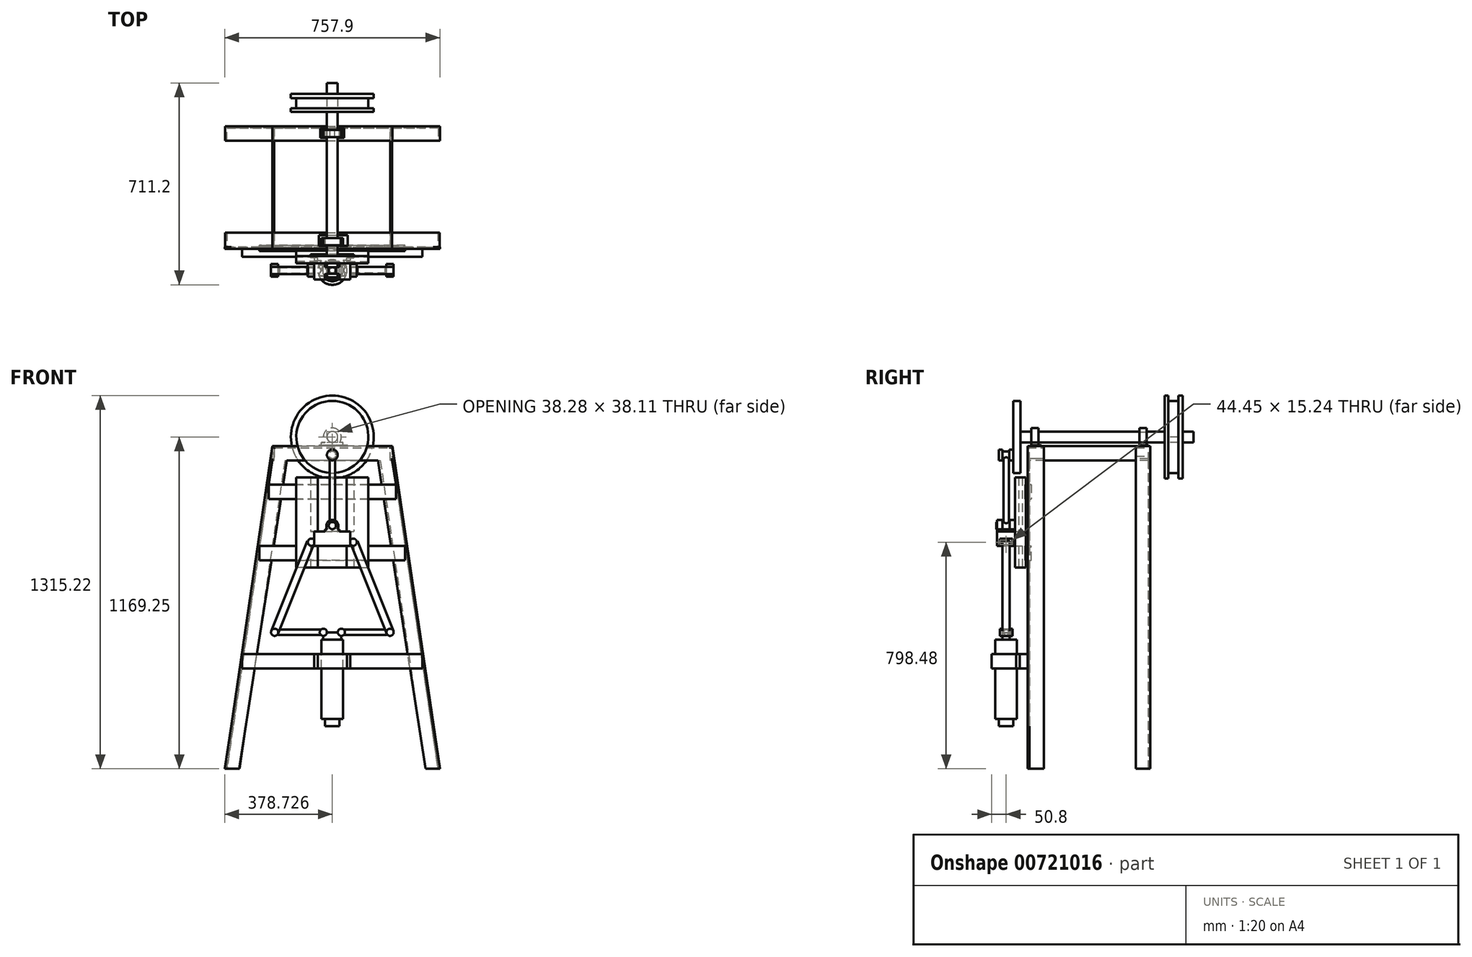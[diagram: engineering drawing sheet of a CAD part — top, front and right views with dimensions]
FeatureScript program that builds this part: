
annotation { "Feature Type Name" : "Feature", "Feature Type Description" : "" }
export const myFeature = defineFeature(function(context is Context, id is Id, definition is map)
    precondition{}
    {
        {
            var Q0;
            Q0=qCreatedBy(makeId("Top.planeOp"),FACE);
            cPlane(context, id + "F0", {"entities" : qUnion([Q0]), "cplaneType" : CPlaneType.OFFSET, "offset" : 127 * mm, "width" : 152.4 * mm, "height" : 152.4 * mm});
        }
        {
            var Q0;
            Q0=qCreatedBy(id+"F0.planeOp",FACE);
            var sketch = newSketch(context, id + "F1", { "sketchPlane" : qUnion([Q0])});
            skLineSegment(sketch, "E0", {"start": v(-31.75, 0) * mm, "end": v(-31.75, 12.7) * mm});
            skLineSegment(sketch, "E1", {"start": v(-31.75, 12.7) * mm, "end": v(-31.75, -12.7) * mm});
            skLineSegment(sketch, "E2", {"start": v(31.75, 0) * mm, "end": v(31.75, 12.7) * mm});
            skLineSegment(sketch, "E3", {"start": v(31.75, 12.7) * mm, "end": v(31.75, -12.7) * mm});
            skLineSegment(sketch, "E4", {"start": v(-31.75, 12.7) * mm, "end": v(31.75, 12.7) * mm});
            skLineSegment(sketch, "E5", {"start": v(-31.75, -12.7) * mm, "end": v(31.75, -12.7) * mm});
            skSolve(sketch);
        }
        {
            var Q0;
            Q0=qCreatedBy(makeId("Front.planeOp"),FACE);
            var sketch = newSketch(context, id + "F2", { "sketchPlane" : qUnion([Q0])});
            skPoint(sketch, "E6", {"position": v(-31.75, 152.4) * mm});
            skPoint(sketch, "E7", {"position": v(31.75, 152.4) * mm});
            skCircle(sketch, "E8", {"center": v(-31.75, 152.4) * mm, "radius": 12.7 * mm});
            skCircle(sketch, "E9", {"center": v(31.75, 152.4) * mm, "radius": 12.7 * mm});
            skSolve(sketch);
        }
        {
            var Q0;
            Q0=qCreatedBy(makeId("Right.planeOp"),FACE);
            cPlane(context, id + "F3", {"entities" : qUnion([Q0]), "cplaneType" : CPlaneType.OFFSET, "offset" : 38.1 * mm, "width" : 152.4 * mm, "height" : 152.4 * mm});
        }
        {
            var Q0;
            Q0=qCreatedBy(makeId("Right.planeOp"),FACE);
            cPlane(context, id + "F4", {"entities" : qUnion([Q0]), "cplaneType" : CPlaneType.OFFSET, "offset" : 38.1 * mm, "oppositeDirection" : true, "width" : 152.4 * mm, "height" : 152.4 * mm});
        }
        {
            var Q0;
            Q0=qCreatedBy(id+"F3.planeOp",FACE);
            var sketch = newSketch(context, id + "F5", { "sketchPlane" : qUnion([Q0])});
            skLineSegment(sketch, "E10", {"start": v(0, 0) * mm, "end": v(0, 152.4) * mm});
            skCircle(sketch, "E11", {"center": v(0, 152.4) * mm, "radius": 9.53 * mm});
            skSolve(sketch);
        }
        {
            var Q0;
            Q0=qCreatedBy(id+"F4.planeOp",FACE);
            var sketch = newSketch(context, id + "F6", { "sketchPlane" : qUnion([Q0])});
            skLineSegment(sketch, "E12", {"start": v(0, 0) * mm, "end": v(0, 152.4) * mm});
            skCircle(sketch, "E13", {"center": v(0, 152.4) * mm, "radius": 9.53 * mm});
            skSolve(sketch);
        }
        {
            var Q0;
            Q0=qCreatedBy(makeId("Top.planeOp"),FACE);
            cPlane(context, id + "F7", {"entities" : qUnion([Q0]), "cplaneType" : CPlaneType.OFFSET, "offset" : 457.2 * mm, "width" : 152.4 * mm, "height" : 152.4 * mm});
        }
        {
            var Q0;
            Q0=qCreatedBy(makeId("Front.planeOp"),FACE);
            var sketch = newSketch(context, id + "F8", { "sketchPlane" : qUnion([Q0])});
            skLineSegment(sketch, "E14", {"start": v(0, 0) * mm, "end": v(-73.66, 0) * mm});
            skLineSegment(sketch, "E15", {"start": v(0, 0) * mm, "end": v(73.66, 0) * mm});
            skLineSegment(sketch, "E16", {"start": v(73.66, 0) * mm, "end": v(73.66, 469.9) * mm});
            skLineSegment(sketch, "E17", {"start": v(-73.66, 0) * mm, "end": v(-73.66, 469.9) * mm});
            skCircle(sketch, "E18", {"center": v(-73.66, 469.9) * mm, "radius": 12.7 * mm});
            skCircle(sketch, "E19", {"center": v(73.66, 469.9) * mm, "radius": 12.7 * mm});
            skSolve(sketch);
        }
        {
            var Q0;
            Q0=qCreatedBy(makeId("Front.planeOp"),FACE);
            var sketch = newSketch(context, id + "F9", { "sketchPlane" : qUnion([Q0])});
            skLineSegment(sketch, "E20", {"start": v(0, 0) * mm, "end": v(88.9, 0) * mm});
            skLineSegment(sketch, "E21", {"start": v(0, 0) * mm, "end": v(203.2, 0) * mm});
            skLineSegment(sketch, "E22", {"start": v(203.2, 0) * mm, "end": v(203.2, 152.4) * mm});
            skLineSegment(sketch, "E23", {"start": v(76.2, 469.9) * mm, "end": v(88.25, 474.72) * mm});
            skLineSegment(sketch, "E24", {"start": v(203.2, 152.4) * mm, "end": v(191.4, 147.68) * mm});
            skLineSegment(sketch, "E25", {"start": v(76.2, 469.9) * mm, "end": v(64.4, 465.18) * mm});
            skLineSegment(sketch, "E26", {"start": v(203.2, 152.4) * mm, "end": v(215, 157.12) * mm});
            skLineSegment(sketch, "E27", {"start": v(88.25, 474.72) * mm, "end": v(215, 157.12) * mm});
            skLineSegment(sketch, "E28", {"start": v(191.4, 147.68) * mm, "end": v(64.4, 465.18) * mm});
            skSolve(sketch);
        }
        {
            var Q0;
            Q0=qCreatedBy(makeId("Front.planeOp"),FACE);
            var sketch = newSketch(context, id + "F10", { "sketchPlane" : qUnion([Q0])});
            skLineSegment(sketch, "E29", {"start": v(0, 0) * mm, "end": v(-76.2, 0) * mm});
            skLineSegment(sketch, "E30", {"start": v(0, 0) * mm, "end": v(-203.2, 0) * mm});
            skLineSegment(sketch, "E31", {"start": v(-203.2, 0) * mm, "end": v(-203.2, 152.4) * mm});
            skLineSegment(sketch, "E32", {"start": v(-76.2, 469.9) * mm, "end": v(-88, 474.62) * mm});
            skLineSegment(sketch, "E33", {"start": v(-88, 474.62) * mm, "end": v(-64.4, 465.18) * mm});
            skLineSegment(sketch, "E34", {"start": v(-203.2, 152.4) * mm, "end": v(-191.4, 147.68) * mm});
            skLineSegment(sketch, "E35", {"start": v(-203.2, 152.4) * mm, "end": v(-215, 157.12) * mm});
            skLineSegment(sketch, "E36", {"start": v(-64.4, 465.18) * mm, "end": v(-191.4, 147.68) * mm});
            skLineSegment(sketch, "E37", {"start": v(-88, 474.62) * mm, "end": v(-215, 157.12) * mm});
            skSolve(sketch);
        }
        {
            var Q0;
            Q0=qCreatedBy(makeId("Front.planeOp"),FACE);
            cPlane(context, id + "F11", {"entities" : qUnion([Q0]), "cplaneType" : CPlaneType.OFFSET, "offset" : 12.7 * mm, "width" : 152.4 * mm, "height" : 152.4 * mm});
        }
        {
            var Q0;
            Q0=qCreatedBy(makeId("Front.planeOp"),FACE);
            cPlane(context, id + "F12", {"entities" : qUnion([Q0]), "cplaneType" : CPlaneType.OFFSET, "offset" : 12.7 * mm, "oppositeDirection" : true, "width" : 152.4 * mm, "height" : 152.4 * mm});
        }
        {
            var Q0;
            Q0=qCreatedBy(id+"F11.planeOp",FACE);
            var sketch = newSketch(context, id + "F13", { "sketchPlane" : qUnion([Q0])});
            skLineSegment(sketch, "E38", {"start": v(0, 508) * mm, "end": v(-25.4, 508) * mm});
            skLineSegment(sketch, "E39", {"start": v(0, 508) * mm, "end": v(25.4, 508) * mm});
            skLineSegment(sketch, "E40", {"start": v(-25.4, 508) * mm, "end": v(-25.4, 515.62) * mm});
            skLineSegment(sketch, "E41", {"start": v(25.4, 508) * mm, "end": v(25.4, 515.62) * mm});
            skLineSegment(sketch, "E42", {"start": v(25.4, 515.62) * mm, "end": v(17.77, 515.62) * mm});
            skLineSegment(sketch, "E43", {"start": v(-25.4, 515.62) * mm, "end": v(-17.78, 515.62) * mm});
            skCircle(sketch, "E44", {"center": v(0, 528.32) * mm, "radius": 12.7 * mm});
            skArc(sketch, "E45", {"start": v(17.77, 515.62) * mm, "mid": v(0, 548.64) * mm, "end": v(-17.78, 515.62) * mm});
            skPoint(sketch, "E46.start.orphan", {"position": v(0, 541.02) * mm});
            skSolve(sketch);
        }
        {
            var Q0;
            Q0=qCreatedBy(id+"F12.planeOp",FACE);
            var sketch = newSketch(context, id + "F14", { "sketchPlane" : qUnion([Q0])});
            skLineSegment(sketch, "E47", {"start": v(0, 508) * mm, "end": v(-25.4, 508) * mm});
            skLineSegment(sketch, "E48", {"start": v(0, 508) * mm, "end": v(25.4, 508) * mm});
            skLineSegment(sketch, "E49", {"start": v(25.4, 508) * mm, "end": v(25.4, 515.62) * mm});
            skLineSegment(sketch, "E50", {"start": v(-25.4, 508) * mm, "end": v(-25.4, 515.62) * mm});
            skLineSegment(sketch, "E51", {"start": v(0, 527.34) * mm, "end": v(0, 528.32) * mm});
            skCircle(sketch, "E52", {"center": v(0, 528.32) * mm, "radius": 12.7 * mm});
            skLineSegment(sketch, "E53", {"start": v(25.4, 515.62) * mm, "end": v(17.78, 515.62) * mm});
            skLineSegment(sketch, "E54", {"start": v(-25.4, 515.62) * mm, "end": v(-17.78, 515.62) * mm});
            skArc(sketch, "E55", {"start": v(17.78, 515.62) * mm, "mid": v(0, 548.64) * mm, "end": v(-17.78, 515.62) * mm});
            skPoint(sketch, "E56.start.orphan", {"position": v(0, 541.02) * mm});
            skSolve(sketch);
        }
        {
            var Q0;
            Q0=qCreatedBy(makeId("Front.planeOp"),FACE);
            var sketch = newSketch(context, id + "F15", { "sketchPlane" : qUnion([Q0])});
            skLineSegment(sketch, "E57", {"start": v(0, 0) * mm, "end": v(0, 528.32) * mm});
            skCircle(sketch, "E58", {"center": v(0, 528.32) * mm, "radius": 12.7 * mm});
            skSolve(sketch);
        }
        {
            var Q0;
            Q0=qCreatedBy(makeId("Front.planeOp"),FACE);
            cPlane(context, id + "F16", {"entities" : qUnion([Q0]), "cplaneType" : CPlaneType.OFFSET, "offset" : 2.54 * mm, "width" : 152.4 * mm, "height" : 152.4 * mm});
        }
        {
            var Q0;
            Q0=qCreatedBy(makeId("Top.planeOp"),FACE);
            cPlane(context, id + "F17", {"entities" : qUnion([Q0]), "cplaneType" : CPlaneType.OFFSET, "offset" : 533.4 * mm, "width" : 152.4 * mm, "height" : 152.4 * mm});
        }
        {
            var Q0;
            Q0=qCreatedBy(id+"F17.planeOp",FACE);
            var sketch = newSketch(context, id + "F18", { "sketchPlane" : qUnion([Q0])});
            skCircle(sketch, "E59", {"center": v(0, 0) * mm, "radius": 9.53 * mm});
            skSolve(sketch);
        }
        {
            var Q0;
            Q0=qCreatedBy(makeId("Front.planeOp"),FACE);
            var sketch = newSketch(context, id + "F19", { "sketchPlane" : qUnion([Q0])});
            skLineSegment(sketch, "E60", {"start": v(0, 0) * mm, "end": v(0, 777.24) * mm});
            skCircle(sketch, "E61", {"center": v(0, 777.24) * mm, "radius": 12.7 * mm});
            skSolve(sketch);
        }
        {
            var Q0;
            Q0=qCreatedBy(makeId("Front.planeOp"),FACE);
            cPlane(context, id + "F20", {"entities" : qUnion([Q0]), "cplaneType" : CPlaneType.OFFSET, "offset" : 25.4 * mm, "oppositeDirection" : true, "width" : 152.4 * mm, "height" : 152.4 * mm});
        }
        {
            var Q0;
            Q0=qCreatedBy(id+"F20.planeOp",FACE);
            var sketch = newSketch(context, id + "F21", { "sketchPlane" : qUnion([Q0])});
            skLineSegment(sketch, "E62", {"start": v(0, 0) * mm, "end": v(0, 713.74) * mm});
            skCircle(sketch, "E63", {"center": v(0, 840.74) * mm, "radius": 127 * mm});
            skCircle(sketch, "E64", {"center": v(0, 777.24) * mm, "radius": 19.05 * mm});
            skLineSegment(sketch, "E65.trimOffspring", {"start": v(0, 796.3) * mm, "end": v(0, 840.74) * mm});
            skLineSegment(sketch, "E66", {"start": v(0, 0) * mm, "end": v(127, 0) * mm});
            skLineSegment(sketch, "E67", {"start": v(0, 777.24) * mm, "end": v(127, 777.24) * mm});
            skLineSegment(sketch, "E68", {"start": v(127, 777.24) * mm, "end": v(127, 0) * mm});
            skCircle(sketch, "E69", {"center": v(0, 840.74) * mm, "radius": 19.05 * mm});
            skLineSegment(sketch, "E70", {"start": v(0, 840.74) * mm, "end": v(19.05, 840.74) * mm});
            skLineSegment(sketch, "E71", {"start": v(0, 0) * mm, "end": v(190.5, 0) * mm});
            skPoint(sketch, "E71.endSnap0", {"position": v(63.5, 0) * mm});
            skLineSegment(sketch, "E72", {"start": v(190.5, 840.74) * mm, "end": v(190.5, 0) * mm});
            skLineSegment(sketch, "E73.trimOffspring", {"start": v(127, 840.74) * mm, "end": v(190.5, 840.74) * mm});
            skSolve(sketch);
        }
        {
            var Q0;
            Q0=qCreatedBy(makeId("Front.planeOp"),FACE);
            cPlane(context, id + "F22", {"entities" : qUnion([Q0]), "cplaneType" : CPlaneType.OFFSET, "offset" : 12.45 * mm, "width" : 152.4 * mm, "height" : 152.4 * mm});
        }
        {
            var Q0;
            Q0=qCreatedBy(id+"F22.planeOp",FACE);
            var sketch = newSketch(context, id + "F23", { "sketchPlane" : qUnion([Q0])});
            skLineSegment(sketch, "E74", {"start": v(0, 0) * mm, "end": v(0, 777.24) * mm});
            skCircle(sketch, "E75", {"center": v(0, 777.24) * mm, "radius": 19.05 * mm});
            skSolve(sketch);
        }
        {
            var Q0;
            Q0=qCreatedBy(makeId("Front.planeOp"),FACE);
            cPlane(context, id + "F24", {"entities" : qUnion([Q0]), "cplaneType" : CPlaneType.OFFSET, "offset" : 88.9 * mm, "oppositeDirection" : true, "width" : 152.4 * mm, "height" : 152.4 * mm});
        }
        {
            var Q0;
            Q0=qCreatedBy(id+"F24.planeOp",FACE);
            var sketch = newSketch(context, id + "F25", { "sketchPlane" : qUnion([Q0])});
            skLineSegment(sketch, "E76", {"start": v(0, 0) * mm, "end": v(0, 808.99) * mm});
            skLineSegment(sketch, "E77", {"start": v(0, 840.23) * mm, "end": v(0, 840.58) * mm});
            skLineSegment(sketch, "E78", {"start": v(19.05, 809) * mm, "end": v(0, 809) * mm});
            skLineSegment(sketch, "E79", {"start": v(0, 809) * mm, "end": v(38.1, 809) * mm});
            skLineSegment(sketch, "E80", {"start": v(0, 809) * mm, "end": v(-38.1, 809) * mm});
            skLineSegment(sketch, "E81", {"start": v(-38.1, 809) * mm, "end": v(-38.1, 821.7) * mm});
            skLineSegment(sketch, "E82", {"start": v(38.1, 809) * mm, "end": v(38.1, 821.7) * mm});
            skLineSegment(sketch, "E83", {"start": v(38.1, 821.7) * mm, "end": v(25.52, 821.7) * mm});
            skArc(sketch, "E84", {"start": v(25.52, 821.7) * mm, "mid": v(0, 872.33) * mm, "end": v(-25.52, 821.7) * mm});
            skLineSegment(sketch, "E85.trimOffspring", {"start": v(0, 821.69) * mm, "end": v(0, 840.23) * mm});
            skLineSegment(sketch, "E86.trimOffspring", {"start": v(-25.52, 821.7) * mm, "end": v(-38.1, 821.7) * mm});
            skPoint(sketch, "E87.start.orphan", {"position": v(-19.05, 809) * mm});
            skLineSegment(sketch, "E88", {"start": v(0, 840.58) * mm, "end": v(0, 859.63) * mm});
            skLineSegment(sketch, "E89", {"start": v(0, 859.63) * mm, "end": v(0, 872.33) * mm});
            skSolve(sketch);
        }
        {
            var Q0;
            Q0=qCreatedBy(makeId("Front.planeOp"),FACE);
            cPlane(context, id + "F26", {"entities" : qUnion([Q0]), "cplaneType" : CPlaneType.OFFSET, "offset" : 76.2 * mm, "oppositeDirection" : true, "width" : 152.4 * mm, "height" : 152.4 * mm});
        }
        {
            var Q0;
            Q0=qCreatedBy(id+"F26.planeOp",FACE);
            var sketch = newSketch(context, id + "F27", { "sketchPlane" : qUnion([Q0])});
            skLineSegment(sketch, "E90", {"start": v(0, 0) * mm, "end": v(0, 757.17) * mm});
            skPoint(sketch, "E91.endSnap0", {"position": v(-76.2, 807.97) * mm});
            skLineSegment(sketch, "E92", {"start": v(-328.08, -328.4) * mm, "end": v(-160.25, 757.17) * mm});
            skLineSegment(sketch, "E93", {"start": v(328.08, -328.4) * mm, "end": v(160.25, 757.17) * mm});
            skLineSegment(sketch, "E94", {"start": v(-203.2, 807.97) * mm, "end": v(-378.88, -328.38) * mm});
            skLineSegment(sketch, "E95", {"start": v(203.2, 807.97) * mm, "end": v(378.88, -328.38) * mm});
            skLineSegment(sketch, "E96", {"start": v(160.25, 757.17) * mm, "end": v(-160.25, 757.17) * mm});
            skLineSegment(sketch, "E97", {"start": v(-160.25, 757.17) * mm, "end": v(160.25, 757.17) * mm});
            skPoint(sketch, "E98.orphan", {"position": v(0, 807.97) * mm});
            skPoint(sketch, "E99.orphan", {"position": v(-152.4, 807.97) * mm});
            skPoint(sketch, "E100.end.orphan", {"position": v(152.4, 807.97) * mm});
            skLineSegment(sketch, "E101", {"start": v(203.2, 807.97) * mm, "end": v(-203.2, 807.97) * mm});
            skLineSegment(sketch, "E102", {"start": v(328.08, -328.4) * mm, "end": v(378.88, -328.38) * mm});
            skLineSegment(sketch, "E103", {"start": v(-378.88, -328.38) * mm, "end": v(-328.08, -328.4) * mm});
            skSolve(sketch);
        }
        {
            var Q0;
            {var subQ3=sQuery(id+"F27.wireOp",EDGE,"E92");Q0=makeQuery(id+"F27.imprint","IMPRINT",FACE,{"disambiguationData":[TD([[makeQuery(id+"F27.imprint","IMPRINT",EDGE,{"derivedFrom":subQ3}),1.0]])]});}
            extrude(context, id + "F28", {"entities" : qUnion([Q0]), "oppositeDirection" : true, "depth" : 6.35 * mm, "offsetDistance" : 25.4 * mm});
        }
        {
            var Q0;
            Q0=qCreatedBy(id+"F26.planeOp",FACE);
            var sketch = newSketch(context, id + "F29", { "sketchPlane" : qUnion([Q0])});
            skLineSegment(sketch, "E104", {"start": v(0, 0) * mm, "end": v(0, 801.63) * mm});
            skLineSegment(sketch, "E105", {"start": v(0, 801.63) * mm, "end": v(0, -177.8) * mm});
            skLineSegment(sketch, "E106", {"start": v(0, 807.97) * mm, "end": v(160.02, 807.97) * mm});
            skLineSegment(sketch, "E107", {"start": v(0, 807.97) * mm, "end": v(-160.02, 807.97) * mm});
            skLineSegment(sketch, "E108", {"start": v(-160.02, 807.97) * mm, "end": v(-210.82, 807.97) * mm});
            skLineSegment(sketch, "E109", {"start": v(160.02, 807.97) * mm, "end": v(210.82, 807.97) * mm});
            skLineSegment(sketch, "E110", {"start": v(210.82, 807.97) * mm, "end": v(377.74, -328.57) * mm});
            skLineSegment(sketch, "E111", {"start": v(-210.82, 807.97) * mm, "end": v(-377.74, -328.57) * mm});
            skLineSegment(sketch, "E112", {"start": v(-205.4, 801.63) * mm, "end": v(-371.4, -328.57) * mm});
            skLineSegment(sketch, "E113", {"start": v(205.4, 801.63) * mm, "end": v(371.4, -328.57) * mm});
            skLineSegment(sketch, "E114", {"start": v(-205.4, 801.63) * mm, "end": v(205.4, 801.63) * mm});
            skPoint(sketch, "E115.orphan", {"position": v(-204.47, 807.97) * mm});
            skLineSegment(sketch, "E116", {"start": v(371.4, -328.57) * mm, "end": v(377.74, -328.57) * mm});
            skLineSegment(sketch, "E117", {"start": v(-377.74, -328.57) * mm, "end": v(-371.4, -328.57) * mm});
            skSolve(sketch);
        }
        {
            var Q0;
            Q0=makeQuery(id+"F29.imprint","IMPRINT",FACE,{"disambiguationData":[TD([[makeQuery(id+"F29.imprint","IMPRINT",EDGE,{"derivedFrom":sQuery(id+"F29.wireOp",EDGE,"E106")}),-1.0]])]});
            extrude(context, id + "F30", {"entities" : qUnion([Q0]), "oppositeDirection" : true, "depth" : 57.15 * mm, "offsetDistance" : 25.4 * mm});
        }
        {
            var Q0;
            Q0=qCreatedBy(id+"F26.planeOp",FACE);
            var sketch = newSketch(context, id + "F31", { "sketchPlane" : qUnion([Q0])});
            skLineSegment(sketch, "E118", {"start": v(-317.5, 50.8) * mm, "end": v(-317.5, 76.2) * mm});
            skLineSegment(sketch, "E119", {"start": v(317.5, 50.8) * mm, "end": v(317.5, 76.2) * mm});
            skLineSegment(sketch, "E120", {"start": v(317.5, 76.2) * mm, "end": v(317.5, 25.4) * mm});
            skLineSegment(sketch, "E121", {"start": v(-317.5, 76.2) * mm, "end": v(-317.5, 25.4) * mm});
            skLineSegment(sketch, "E122", {"start": v(-317.5, 25.4) * mm, "end": v(317.5, 25.4) * mm});
            skLineSegment(sketch, "E123", {"start": v(317.5, 76.2) * mm, "end": v(-317.5, 76.2) * mm});
            skSolve(sketch);
        }
        {
            var Q0;
            {var subQ2=sQuery(id+"F31.wireOp",EDGE,"E122");Q0=makeQuery(id+"F31.imprint","IMPRINT",FACE,{"disambiguationData":[TD([[makeQuery(id+"F31.imprint","IMPRINT",EDGE,{"derivedFrom":subQ2}),1.0]])]});}
            extrude(context, id + "F32", {"entities" : qUnion([Q0]), "operationType" : NewBodyOperationType.ADD, "depth" : 27.94 * mm, "offsetDistance" : 25.4 * mm});
        }
        {
            var Q0;
            Q0=qCreatedBy(makeId("Top.planeOp"),FACE);
            cPlane(context, id + "F33", {"entities" : qUnion([Q0]), "cplaneType" : CPlaneType.OFFSET, "offset" : 75.95 * mm, "width" : 152.4 * mm, "height" : 152.4 * mm});
        }
        {
            var Q0;
            Q0=qCreatedBy(id+"F33.planeOp",FACE);
            var sketch = newSketch(context, id + "F34", { "sketchPlane" : qUnion([Q0])});
            skCircle(sketch, "E124", {"center": v(0, 0) * mm, "radius": 38.1 * mm});
            skLineSegment(sketch, "E125", {"start": v(0, 0) * mm, "end": v(0, 38.1) * mm});
            skLineSegment(sketch, "E126", {"start": v(0, 50.8) * mm, "end": v(-63.5, 50.8) * mm});
            skLineSegment(sketch, "E127", {"start": v(0, 50.8) * mm, "end": v(63.5, 50.8) * mm});
            skLineSegment(sketch, "E128", {"start": v(63.5, 50.8) * mm, "end": v(63.5, 35.56) * mm});
            skLineSegment(sketch, "E129", {"start": v(-63.5, 50.8) * mm, "end": v(-63.5, 35.56) * mm});
            skLineSegment(sketch, "E130", {"start": v(-63.5, 35.56) * mm, "end": v(-38.1, 35.56) * mm});
            skLineSegment(sketch, "E131", {"start": v(63.5, 35.56) * mm, "end": v(38.1, 35.56) * mm});
            skArc(sketch, "E132", {"start": v(-38.1, 35.56) * mm, "mid": v(0, -50.8) * mm, "end": v(38.1, 35.56) * mm});
            skPoint(sketch, "E133.start.orphan", {"position": v(0, -38.1) * mm});
            skSolve(sketch);
        }
        {
            var Q0;
            Q0=makeQuery(id+"F34.imprint","IMPRINT",FACE,{"disambiguationData":[TD([[makeQuery(id+"F34.imprint","IMPRINT",EDGE,{"derivedFrom":sQuery(id+"F34.wireOp",EDGE,"E124")}),-1.0]])]});
            extrude(context, id + "F35", {"entities" : qUnion([Q0]), "operationType" : NewBodyOperationType.ADD, "oppositeDirection" : true, "depth" : 50.8 * mm, "offsetDistance" : 25.4 * mm});
        }
        {
            var Q0;
            Q0=qCreatedBy(makeId("Front.planeOp"),FACE);
            var sketch = newSketch(context, id + "F36", { "sketchPlane" : qUnion([Q0])});
            skLineSegment(sketch, "E134", {"start": v(0, 0) * mm, "end": v(-203.2, 0) * mm});
            skLineSegment(sketch, "E135", {"start": v(-203.2, 0) * mm, "end": v(-203.2, 152.4) * mm});
            skCircle(sketch, "E136", {"center": v(-203.2, 152.4) * mm, "radius": 12.7 * mm});
            skLineSegment(sketch, "E137", {"start": v(0, 0) * mm, "end": v(203.2, 0) * mm});
            skLineSegment(sketch, "E138", {"start": v(203.2, 0) * mm, "end": v(203.2, 152.4) * mm});
            skCircle(sketch, "E139", {"center": v(203.2, 152.4) * mm, "radius": 12.7 * mm});
            skSolve(sketch);
        }
        {
            var Q0;
            Q0=qCreatedBy(makeId("Top.planeOp"),FACE);
            var sketch = newSketch(context, id + "F37", { "sketchPlane" : qUnion([Q0])});
            skCircle(sketch, "E140", {"center": v(0, 0) * mm, "radius": 25.4 * mm});
            skCircle(sketch, "E141", {"center": v(0, 0) * mm, "radius": 38.1 * mm});
            skSolve(sketch);
        }
        {
            var Q0;
            Q0=makeQuery(id+"F37.imprint","IMPRINT",FACE,{"disambiguationData":[TD([[makeQuery(id+"F37.imprint","IMPRINT",EDGE,{"derivedFrom":sQuery(id+"F37.wireOp",EDGE,"E140")}),-1.0]])]});
            extrude(context, id + "F38", {"entities" : qUnion([Q0]), "operationType" : NewBodyOperationType.ADD, "depth" : 127 * mm, "offsetDistance" : 25.4 * mm});
        }
        {
            var Q0;
            Q0=makeQuery(id+"F37.imprint","IMPRINT",FACE,{"disambiguationData":[TD([[makeQuery(id+"F37.imprint","IMPRINT",EDGE,{"derivedFrom":sQuery(id+"F37.wireOp",EDGE,"E140")}),-1.0]])]});
            extrude(context, id + "F39", {"entities" : qUnion([Q0]), "operationType" : NewBodyOperationType.ADD, "oppositeDirection" : true, "depth" : 152.4 * mm, "offsetDistance" : 25.4 * mm});
        }
        {
            var Q0;
            Q0=qCreatedBy(makeId("Front.planeOp"),FACE);
            cPlane(context, id + "F40", {"entities" : qUnion([Q0]), "cplaneType" : CPlaneType.OFFSET, "offset" : 88.9 * mm, "oppositeDirection" : true, "width" : 152.4 * mm, "height" : 152.4 * mm});
        }
        {
            var Q0;
            Q0=qCreatedBy(id+"F40.planeOp",FACE);
            var sketch = newSketch(context, id + "F41", { "sketchPlane" : qUnion([Q0])});
            skLineSegment(sketch, "E142", {"start": v(0, 457.2) * mm, "end": v(-256.54, 457.2) * mm});
            skLineSegment(sketch, "E143", {"start": v(0, 406.4) * mm, "end": v(-256.54, 406.4) * mm});
            skLineSegment(sketch, "E144", {"start": v(-256.54, 406.4) * mm, "end": v(-256.54, 457.2) * mm});
            skLineSegment(sketch, "E145", {"start": v(0, 457.2) * mm, "end": v(256.54, 457.2) * mm});
            skLineSegment(sketch, "E146", {"start": v(0, 406.4) * mm, "end": v(256.54, 406.4) * mm});
            skLineSegment(sketch, "E147", {"start": v(256.54, 406.4) * mm, "end": v(256.54, 457.2) * mm});
            skLineSegment(sketch, "E148", {"start": v(-29.14, 673.22) * mm, "end": v(0, 673.22) * mm});
            skLineSegment(sketch, "E149", {"start": v(0, 673.22) * mm, "end": v(-224.3, 673.22) * mm});
            skLineSegment(sketch, "E150", {"start": v(-224.3, 673.22) * mm, "end": v(-224.3, 622.42) * mm});
            skLineSegment(sketch, "E151", {"start": v(-224.3, 622.42) * mm, "end": v(-29.14, 622.42) * mm});
            skLineSegment(sketch, "E152", {"start": v(-224.3, 622.42) * mm, "end": v(0, 622.42) * mm});
            skLineSegment(sketch, "E153", {"start": v(0, 673.22) * mm, "end": v(224.3, 673.22) * mm});
            skLineSegment(sketch, "E154", {"start": v(0, 622.42) * mm, "end": v(224.3, 622.42) * mm});
            skLineSegment(sketch, "E155", {"start": v(224.3, 673.22) * mm, "end": v(224.3, 622.42) * mm});
            skSolve(sketch);
        }
        {
            var Q0;
            {var subQ2=sQuery(id+"F41.wireOp",EDGE,"E150");Q0=makeQuery(id+"F41.imprint","IMPRINT",FACE,{"disambiguationData":[TD([[makeQuery(id+"F41.imprint","IMPRINT",EDGE,{"derivedFrom":subQ2}),1.0]])]});}
            extrude(context, id + "F42", {"entities" : qUnion([Q0]), "operationType" : NewBodyOperationType.ADD, "depth" : 20.32 * mm, "offsetDistance" : 25.4 * mm});
        }
        {
            var Q0;
            Q0=makeQuery(id+"F41.imprint","IMPRINT",FACE,{"disambiguationData":[TD([[makeQuery(id+"F41.imprint","IMPRINT",EDGE,{"derivedFrom":sQuery(id+"F41.wireOp",EDGE,"E142")}),1.0]])]});
            extrude(context, id + "F43", {"entities" : qUnion([Q0]), "operationType" : NewBodyOperationType.ADD, "depth" : 20.32 * mm, "offsetDistance" : 25.4 * mm});
        }
        {
            var Q0;
            Q0=qCreatedBy(makeId("Top.planeOp"),FACE);
            cPlane(context, id + "F44", {"entities" : qUnion([Q0]), "cplaneType" : CPlaneType.OFFSET, "offset" : 381 * mm, "width" : 152.4 * mm, "height" : 152.4 * mm});
        }
        {
            var Q0;
            Q0=qCreatedBy(id+"F44.planeOp",FACE);
            var sketch = newSketch(context, id + "F45", { "sketchPlane" : qUnion([Q0])});
            skLineSegment(sketch, "E156", {"start": v(0, 0) * mm, "end": v(0, 56.9) * mm});
            skLineSegment(sketch, "E157", {"start": v(0, 56.9) * mm, "end": v(-76.2, 56.9) * mm});
            skLineSegment(sketch, "E158", {"start": v(0, 56.9) * mm, "end": v(76.2, 56.9) * mm});
            skLineSegment(sketch, "E159", {"start": v(76.2, 56.9) * mm, "end": v(76.2, 44.2) * mm});
            skLineSegment(sketch, "E160", {"start": v(-76.2, 56.9) * mm, "end": v(-76.2, 44.2) * mm});
            skLineSegment(sketch, "E161", {"start": v(-76.2, 44.2) * mm, "end": v(-50.8, 44.2) * mm});
            skLineSegment(sketch, "E162", {"start": v(76.2, 44.2) * mm, "end": v(50.8, 44.2) * mm});
            skLineSegment(sketch, "E163", {"start": v(50.8, 44.2) * mm, "end": v(50.8, 31.5) * mm});
            skLineSegment(sketch, "E164", {"start": v(-50.8, 44.2) * mm, "end": v(-50.8, 31.5) * mm});
            skLineSegment(sketch, "E165", {"start": v(-50.8, 31.5) * mm, "end": v(-127, 31.5) * mm});
            skLineSegment(sketch, "E166", {"start": v(50.8, 31.5) * mm, "end": v(127, 31.5) * mm});
            skLineSegment(sketch, "E167", {"start": v(127, 31.5) * mm, "end": v(127, 69.6) * mm});
            skLineSegment(sketch, "E168", {"start": v(-127, 31.5) * mm, "end": v(-127, 69.6) * mm});
            skLineSegment(sketch, "E169", {"start": v(-127, 69.6) * mm, "end": v(127, 69.6) * mm});
            skSolve(sketch);
        }
        {
            var Q0;
            Q0=makeQuery(id+"F45.imprint","IMPRINT",FACE,{"disambiguationData":[TD([[makeQuery(id+"F45.imprint","IMPRINT",EDGE,{"derivedFrom":sQuery(id+"F45.wireOp",EDGE,"E157")}),-1.0]])]});
            extrude(context, id + "F46", {"entities" : qUnion([Q0]), "operationType" : NewBodyOperationType.ADD, "depth" : 317.5 * mm, "offsetDistance" : 25.4 * mm});
        }
        {
            var Q0;
            Q0=qCreatedBy(id+"F26.planeOp",FACE);
            var sketch = newSketch(context, id + "F47", { "sketchPlane" : qUnion([Q0])});
            skLineSegment(sketch, "E170", {"start": v(0, 0) * mm, "end": v(0, 801.62) * mm});
            skLineSegment(sketch, "E171", {"start": v(0, 807.97) * mm, "end": v(-210.82, 807.97) * mm});
            skLineSegment(sketch, "E172", {"start": v(0, 807.97) * mm, "end": v(210.82, 807.97) * mm});
            skLineSegment(sketch, "E173", {"start": v(210.82, 807.97) * mm, "end": v(210.82, 757.17) * mm});
            skLineSegment(sketch, "E174", {"start": v(-210.82, 807.97) * mm, "end": v(-210.82, 757.17) * mm});
            skLineSegment(sketch, "E175", {"start": v(-210.82, 757.17) * mm, "end": v(-204.47, 757.17) * mm});
            skLineSegment(sketch, "E176", {"start": v(-204.47, 801.62) * mm, "end": v(-204.47, 757.17) * mm});
            skLineSegment(sketch, "E177", {"start": v(210.82, 757.17) * mm, "end": v(204.47, 757.17) * mm});
            skLineSegment(sketch, "E178", {"start": v(204.47, 757.17) * mm, "end": v(204.47, 801.62) * mm});
            skLineSegment(sketch, "E179", {"start": v(196.68, 801.62) * mm, "end": v(204.47, 801.62) * mm});
            skLineSegment(sketch, "E180", {"start": v(204.47, 801.62) * mm, "end": v(-204.47, 801.62) * mm});
            skPoint(sketch, "E181.orphan", {"position": v(-204.47, 807.97) * mm});
            skPoint(sketch, "E182.orphan", {"position": v(204.47, 807.97) * mm});
            skLineSegment(sketch, "E183", {"start": v(-204.47, 801.62) * mm, "end": v(-204.47, 807.97) * mm});
            skLineSegment(sketch, "E184", {"start": v(204.47, 801.62) * mm, "end": v(204.47, 807.97) * mm});
            skSolve(sketch);
        }
        {
            var Q0;
            Q0=qCreatedBy(id+"F7.planeOp",FACE);
            var sketch = newSketch(context, id + "F48", { "sketchPlane" : qUnion([Q0])});
            skLineSegment(sketch, "E185", {"start": v(0, 31.5) * mm, "end": v(-50.8, 31.5) * mm});
            skLineSegment(sketch, "E186", {"start": v(0, 31.5) * mm, "end": v(50.8, 31.5) * mm});
            skLineSegment(sketch, "E187", {"start": v(50.8, 31.5) * mm, "end": v(50.8, 44.2) * mm});
            skLineSegment(sketch, "E188", {"start": v(-50.8, 31.5) * mm, "end": v(-50.8, 44.2) * mm});
            skLineSegment(sketch, "E189", {"start": v(-50.8, 44.2) * mm, "end": v(-76.2, 44.2) * mm});
            skLineSegment(sketch, "E190", {"start": v(50.8, 44.2) * mm, "end": v(76.2, 44.2) * mm});
            skLineSegment(sketch, "E191", {"start": v(76.2, 44.2) * mm, "end": v(76.2, 56.9) * mm});
            skLineSegment(sketch, "E192", {"start": v(-76.2, 44.2) * mm, "end": v(-76.2, 56.9) * mm});
            skLineSegment(sketch, "E193", {"start": v(-76.2, 56.9) * mm, "end": v(76.2, 56.9) * mm});
            skSolve(sketch);
        }
        {
            var Q0;
            Q0=makeQuery(id+"F48.imprint","IMPRINT",FACE,{"disambiguationData":[TD([[makeQuery(id+"F48.imprint","IMPRINT",EDGE,{"derivedFrom":sQuery(id+"F48.wireOp",EDGE,"E185")}),-1.0]])]});
            extrude(context, id + "F49", {"entities" : qUnion([Q0]), "operationType" : NewBodyOperationType.ADD, "depth" : 50.8 * mm, "offsetDistance" : 25.4 * mm});
        }
        {
            var Q0;
            Q0=qCreatedBy(id+"F7.planeOp",FACE);
            var sketch = newSketch(context, id + "F50", { "sketchPlane" : qUnion([Q0])});
            skLineSegment(sketch, "E194", {"start": v(-63.5, 0) * mm, "end": v(-63.5, 31.75) * mm});
            skLineSegment(sketch, "E195", {"start": v(-63.5, 31.75) * mm, "end": v(-63.5, -31.75) * mm});
            skLineSegment(sketch, "E196", {"start": v(63.5, 0) * mm, "end": v(63.5, 31.75) * mm});
            skLineSegment(sketch, "E197", {"start": v(63.5, 31.75) * mm, "end": v(63.5, -31.75) * mm});
            skLineSegment(sketch, "E198", {"start": v(-63.5, 31.75) * mm, "end": v(63.5, 31.75) * mm});
            skLineSegment(sketch, "E199", {"start": v(-63.5, -31.75) * mm, "end": v(63.5, -31.75) * mm});
            skSolve(sketch);
        }
        {
            var Q0;
            {var subQ0=sQuery(id+"F50.wireOp",EDGE,"E198");Q0=makeQuery(id+"F50.imprint","IMPRINT",FACE,{"disambiguationData":[TD([[makeQuery(id+"F50.imprint","IMPRINT",EDGE,{"derivedFrom":subQ0}),-1.0]])]});}
            extrude(context, id + "F51", {"entities" : qUnion([Q0]), "operationType" : NewBodyOperationType.ADD, "depth" : 50.8 * mm, "offsetDistance" : 25.4 * mm});
        }
        {
            var Q0;
            Q0=makeQuery(id+"F8.imprint","IMPRINT",FACE,{"disambiguationData":[TD([[makeQuery(id+"F8.imprint","IMPRINT",EDGE,{"derivedFrom":sQuery(id+"F8.wireOp",EDGE,"E18")}),1.0]])]});
            var Q1;
            Q1=sQuery(id+"F8.wireOp",EDGE,"E18");
            extrude(context, id + "F52", {"entities" : qUnion([Q0]), "operationType" : NewBodyOperationType.ADD, "surfaceEntities" : qUnion([Q1]), "depth" : 22.22 * mm, "offsetDistance" : 25.4 * mm});
        }
        {
            var Q0;
            Q0=makeQuery(id+"F8.imprint","IMPRINT",FACE,{"disambiguationData":[TD([[makeQuery(id+"F8.imprint","IMPRINT",EDGE,{"derivedFrom":sQuery(id+"F8.wireOp",EDGE,"E18")}),1.0]])]});
            var Q1;
            Q1=sQuery(id+"F8.wireOp",EDGE,"E18");
            extrude(context, id + "F53", {"entities" : qUnion([Q0]), "operationType" : NewBodyOperationType.ADD, "surfaceOperationType" : NewSurfaceOperationType.ADD, "surfaceEntities" : qUnion([Q1]), "oppositeDirection" : true, "depth" : 22.22 * mm, "offsetDistance" : 25.4 * mm});
        }
        {
            var Q0;
            Q0=makeQuery(id+"F8.imprint","IMPRINT",FACE,{"disambiguationData":[TD([[makeQuery(id+"F8.imprint","IMPRINT",EDGE,{"derivedFrom":sQuery(id+"F8.wireOp",EDGE,"E19")}),1.0]])]});
            var Q1;
            Q1=sQuery(id+"F8.wireOp",EDGE,"E19");
            extrude(context, id + "F54", {"entities" : qUnion([Q0]), "operationType" : NewBodyOperationType.ADD, "surfaceEntities" : qUnion([Q1]), "depth" : 22.22 * mm, "offsetDistance" : 25.4 * mm});
        }
        {
            var Q0;
            Q0=makeQuery(id+"F8.imprint","IMPRINT",FACE,{"disambiguationData":[TD([[makeQuery(id+"F8.imprint","IMPRINT",EDGE,{"derivedFrom":sQuery(id+"F8.wireOp",EDGE,"E19")}),1.0]])]});
            var Q1;
            Q1=sQuery(id+"F8.wireOp",EDGE,"E19");
            extrude(context, id + "F55", {"entities" : qUnion([Q0]), "operationType" : NewBodyOperationType.ADD, "surfaceOperationType" : NewSurfaceOperationType.ADD, "surfaceEntities" : qUnion([Q1]), "oppositeDirection" : true, "depth" : 22.22 * mm, "offsetDistance" : 25.4 * mm});
        }
        {
            var Q0;
            Q0=makeQuery(id+"F9.imprint","IMPRINT",FACE,{"disambiguationData":[TD([[makeQuery(id+"F9.imprint","IMPRINT",EDGE,{"derivedFrom":sQuery(id+"F9.wireOp",EDGE,"E23")}),-1.0]])]});
            extrude(context, id + "F56", {"entities" : qUnion([Q0]), "operationType" : NewBodyOperationType.ADD, "depth" : 12.7 * mm, "offsetDistance" : 25.4 * mm});
        }
        {
            var Q0;
            Q0=makeQuery(id+"F9.imprint","IMPRINT",FACE,{"disambiguationData":[TD([[makeQuery(id+"F9.imprint","IMPRINT",EDGE,{"derivedFrom":sQuery(id+"F9.wireOp",EDGE,"E23")}),-1.0]])]});
            extrude(context, id + "F57", {"entities" : qUnion([Q0]), "operationType" : NewBodyOperationType.ADD, "oppositeDirection" : true, "depth" : 12.7 * mm, "offsetDistance" : 25.4 * mm});
        }
        {
            var Q0;
            Q0=makeQuery(id+"F10.imprint","IMPRINT",FACE,{"disambiguationData":[TD([[makeQuery(id+"F10.imprint","IMPRINT",EDGE,{"derivedFrom":sQuery(id+"F10.wireOp",EDGE,"E34")}),1.0]])]});
            extrude(context, id + "F58", {"entities" : qUnion([Q0]), "operationType" : NewBodyOperationType.ADD, "depth" : 12.7 * mm, "offsetDistance" : 25.4 * mm});
        }
        {
            var Q0;
            Q0=makeQuery(id+"F10.imprint","IMPRINT",FACE,{"disambiguationData":[TD([[makeQuery(id+"F10.imprint","IMPRINT",EDGE,{"derivedFrom":sQuery(id+"F10.wireOp",EDGE,"E34")}),1.0]])]});
            extrude(context, id + "F59", {"entities" : qUnion([Q0]), "operationType" : NewBodyOperationType.ADD, "oppositeDirection" : true, "depth" : 12.7 * mm, "offsetDistance" : 25.4 * mm});
        }
        {
            var Q0;
            Q0=makeQuery(id+"F36.imprint","IMPRINT",FACE,{"disambiguationData":[TD([[makeQuery(id+"F36.imprint","IMPRINT",EDGE,{"derivedFrom":sQuery(id+"F36.wireOp",EDGE,"E136")}),1.0]])]});
            var Q1;
            Q1=sQuery(id+"F36.wireOp",EDGE,"E136");
            extrude(context, id + "F60", {"entities" : qUnion([Q0]), "operationType" : NewBodyOperationType.ADD, "surfaceEntities" : qUnion([Q1]), "depth" : 22.22 * mm, "offsetDistance" : 25.4 * mm});
        }
        {
            var Q0;
            Q0=makeQuery(id+"F36.imprint","IMPRINT",FACE,{"disambiguationData":[TD([[makeQuery(id+"F36.imprint","IMPRINT",EDGE,{"derivedFrom":sQuery(id+"F36.wireOp",EDGE,"E136")}),1.0]])]});
            var Q1;
            Q1=sQuery(id+"F36.wireOp",EDGE,"E136");
            extrude(context, id + "F61", {"entities" : qUnion([Q0]), "operationType" : NewBodyOperationType.ADD, "surfaceOperationType" : NewSurfaceOperationType.ADD, "surfaceEntities" : qUnion([Q1]), "oppositeDirection" : true, "depth" : 22.22 * mm, "offsetDistance" : 25.4 * mm});
        }
        {
            var Q0;
            Q0=makeQuery(id+"F36.imprint","IMPRINT",FACE,{"disambiguationData":[TD([[makeQuery(id+"F36.imprint","IMPRINT",EDGE,{"derivedFrom":sQuery(id+"F36.wireOp",EDGE,"E139")}),1.0]])]});
            var Q1;
            Q1=sQuery(id+"F36.wireOp",EDGE,"E139");
            extrude(context, id + "F62", {"entities" : qUnion([Q0]), "operationType" : NewBodyOperationType.ADD, "surfaceEntities" : qUnion([Q1]), "depth" : 22.22 * mm, "offsetDistance" : 25.4 * mm});
        }
        {
            var Q0;
            Q0=makeQuery(id+"F36.imprint","IMPRINT",FACE,{"disambiguationData":[TD([[makeQuery(id+"F36.imprint","IMPRINT",EDGE,{"derivedFrom":sQuery(id+"F36.wireOp",EDGE,"E139")}),1.0]])]});
            var Q1;
            Q1=sQuery(id+"F36.wireOp",EDGE,"E139");
            extrude(context, id + "F63", {"entities" : qUnion([Q0]), "operationType" : NewBodyOperationType.ADD, "surfaceOperationType" : NewSurfaceOperationType.ADD, "surfaceEntities" : qUnion([Q1]), "oppositeDirection" : true, "depth" : 22.22 * mm, "offsetDistance" : 25.4 * mm});
        }
        {
            var Q0;
            {var subQ0=sQuery(id+"F1.wireOp",EDGE,"E4");Q0=makeQuery(id+"F1.imprint","IMPRINT",FACE,{"disambiguationData":[TD([[makeQuery(id+"F1.imprint","IMPRINT",EDGE,{"derivedFrom":subQ0}),-1.0]])]});}
            extrude(context, id + "F64", {"entities" : qUnion([Q0]), "operationType" : NewBodyOperationType.ADD, "depth" : 25.4 * mm, "offsetDistance" : 25.4 * mm});
        }
        {
            var Q0;
            Q0=makeQuery(id+"F2.imprint","IMPRINT",FACE,{"disambiguationData":[TD([[makeQuery(id+"F2.imprint","IMPRINT",EDGE,{"derivedFrom":sQuery(id+"F2.wireOp",EDGE,"E9")}),1.0]])]});
            extrude(context, id + "F65", {"entities" : qUnion([Q0]), "operationType" : NewBodyOperationType.ADD, "depth" : 19.05 * mm, "offsetDistance" : 25.4 * mm});
        }
        {
            var Q0;
            Q0=makeQuery(id+"F2.imprint","IMPRINT",FACE,{"disambiguationData":[TD([[makeQuery(id+"F2.imprint","IMPRINT",EDGE,{"derivedFrom":sQuery(id+"F2.wireOp",EDGE,"E9")}),1.0]])]});
            extrude(context, id + "F66", {"entities" : qUnion([Q0]), "operationType" : NewBodyOperationType.ADD, "oppositeDirection" : true, "depth" : 19.05 * mm, "offsetDistance" : 25.4 * mm});
        }
        {
            var Q0;
            Q0=makeQuery(id+"F2.imprint","IMPRINT",FACE,{"disambiguationData":[TD([[makeQuery(id+"F2.imprint","IMPRINT",EDGE,{"derivedFrom":sQuery(id+"F2.wireOp",EDGE,"E8")}),1.0]])]});
            extrude(context, id + "F67", {"entities" : qUnion([Q0]), "operationType" : NewBodyOperationType.ADD, "depth" : 19.05 * mm, "offsetDistance" : 25.4 * mm});
        }
        {
            var Q0;
            Q0=makeQuery(id+"F2.imprint","IMPRINT",FACE,{"disambiguationData":[TD([[makeQuery(id+"F2.imprint","IMPRINT",EDGE,{"derivedFrom":sQuery(id+"F2.wireOp",EDGE,"E8")}),1.0]])]});
            extrude(context, id + "F68", {"entities" : qUnion([Q0]), "operationType" : NewBodyOperationType.ADD, "oppositeDirection" : true, "depth" : 19.05 * mm, "offsetDistance" : 25.4 * mm});
        }
        {
            var Q0;
            Q0=makeQuery(id+"F5.imprint","IMPRINT",FACE,{"disambiguationData":[TD([[makeQuery(id+"F5.imprint","IMPRINT",EDGE,{"derivedFrom":sQuery(id+"F5.wireOp",EDGE,"E11")}),1.0]])]});
            var Q1;
            Q1=sQuery(id+"F5.wireOp",EDGE,"E11");
            extrude(context, id + "F69", {"entities" : qUnion([Q0]), "operationType" : NewBodyOperationType.ADD, "surfaceEntities" : qUnion([Q1]), "depth" : 152.4 * mm, "offsetDistance" : 25.4 * mm});
        }
        {
            var Q0;
            Q0=makeQuery(id+"F6.imprint","IMPRINT",FACE,{"disambiguationData":[TD([[makeQuery(id+"F6.imprint","IMPRINT",EDGE,{"derivedFrom":sQuery(id+"F6.wireOp",EDGE,"E13")}),1.0]])]});
            var Q1;
            Q1=sQuery(id+"F6.wireOp",EDGE,"E13");
            extrude(context, id + "F70", {"entities" : qUnion([Q0]), "operationType" : NewBodyOperationType.ADD, "surfaceEntities" : qUnion([Q1]), "oppositeDirection" : true, "depth" : 152.4 * mm, "offsetDistance" : 25.4 * mm});
        }
        {
            var Q0;
            Q0=makeQuery(id+"F13.imprint","IMPRINT",FACE,{"disambiguationData":[TD([[makeQuery(id+"F13.imprint","IMPRINT",EDGE,{"derivedFrom":sQuery(id+"F13.wireOp",EDGE,"E38")}),-1.0]])]});
            extrude(context, id + "F71", {"entities" : qUnion([Q0]), "operationType" : NewBodyOperationType.ADD, "depth" : 19.05 * mm, "offsetDistance" : 25.4 * mm});
        }
        {
            var Q0;
            Q0=makeQuery(id+"F14.imprint","IMPRINT",FACE,{"disambiguationData":[TD([[makeQuery(id+"F14.imprint","IMPRINT",EDGE,{"derivedFrom":sQuery(id+"F14.wireOp",EDGE,"E47")}),-1.0]])]});
            extrude(context, id + "F72", {"entities" : qUnion([Q0]), "operationType" : NewBodyOperationType.ADD, "oppositeDirection" : true, "depth" : 19.05 * mm, "offsetDistance" : 25.4 * mm});
        }
        {
            var Q0;
            Q0=makeQuery(id+"F15.imprint","IMPRINT",FACE,{"disambiguationData":[TD([[makeQuery(id+"F15.imprint","IMPRINT",EDGE,{"derivedFrom":sQuery(id+"F15.wireOp",EDGE,"E58")}),1.0]])]});
            extrude(context, id + "F73", {"entities" : qUnion([Q0]), "operationType" : NewBodyOperationType.ADD, "depth" : 34.3 * mm, "offsetDistance" : 25.4 * mm});
        }
        {
            var Q0;
            Q0=makeQuery(id+"F73.opExtrude","CAP_FACE",FACE,{"disambiguationData":[OSD([sQuery(id+"F15.wireOp",EDGE,"E58")])],"isStart":true});
            extrude(context, id + "F74", {"entities" : qUnion([Q0]), "operationType" : NewBodyOperationType.ADD, "depth" : 34.04 * mm, "offsetDistance" : 25.4 * mm});
        }
        {
            var Q0;
            Q0 = qSketchRegion(id + "F18", true);
            var Q1;
            Q1=sQuery(id+"F18.wireOp",EDGE,"E59");
            extrude(context, id + "F75", {"entities" : qUnion([Q0]), "operationType" : NewBodyOperationType.ADD, "surfaceOperationType" : NewSurfaceOperationType.ADD, "surfaceEntities" : qUnion([Q1]), "depth" : 236.22 * mm, "offsetDistance" : 25.4 * mm});
        }
        {
            var Q0;
            Q0=makeQuery(id+"F19.imprint","IMPRINT",FACE,{"disambiguationData":[TD([[makeQuery(id+"F19.imprint","IMPRINT",EDGE,{"derivedFrom":sQuery(id+"F19.wireOp",EDGE,"E61")}),1.0]])]});
            extrude(context, id + "F76", {"entities" : qUnion([Q0]), "operationType" : NewBodyOperationType.ADD, "oppositeDirection" : true, "depth" : 12.7 * mm, "offsetDistance" : 25.4 * mm});
        }
        {
            var Q0;
            Q0=makeQuery(id+"F19.imprint","IMPRINT",FACE,{"disambiguationData":[TD([[makeQuery(id+"F19.imprint","IMPRINT",EDGE,{"derivedFrom":sQuery(id+"F19.wireOp",EDGE,"E61")}),1.0]])]});
            extrude(context, id + "F77", {"entities" : qUnion([Q0]), "operationType" : NewBodyOperationType.ADD, "depth" : 12.7 * mm, "offsetDistance" : 25.4 * mm});
        }
        {
            var Q0;
            {var subQ0=sQuery(id+"F21.wireOp",EDGE,"E64");var subQ1=makeQuery(id+"F21.imprint","IMPRINT",VERTEX,{"disambiguationData":[OD(0.0)],"derivedFrom":subQ0});Q0=makeQuery(id+"F21.imprint","IMPRINT",FACE,{"disambiguationData":[TD([[makeQuery(id+"F21.imprint","IMPRINT",EDGE,{"disambiguationData":[TD([[subQ1,1.0]])],"derivedFrom":subQ0}),1.0]])]});}
            extrude(context, id + "F78", {"entities" : qUnion([Q0]), "operationType" : NewBodyOperationType.ADD, "depth" : 13.97 * mm, "offsetDistance" : 25.4 * mm});
        }
        {
            var Q0;
            {var subQ0=sQuery(id+"F21.wireOp",EDGE,"E64");var subQ1=makeQuery(id+"F21.imprint","IMPRINT",VERTEX,{"disambiguationData":[OD(0.0)],"derivedFrom":subQ0});Q0=makeQuery(id+"F21.imprint","IMPRINT",FACE,{"disambiguationData":[TD([[makeQuery(id+"F21.imprint","IMPRINT",EDGE,{"disambiguationData":[TD([[subQ1,1.0]])],"derivedFrom":subQ0}),1.0]])]});}
            extrude(context, id + "F79", {"entities" : qUnion([Q0]), "operationType" : NewBodyOperationType.ADD, "oppositeDirection" : true, "depth" : 25.4 * mm, "offsetDistance" : 25.4 * mm});
        }
        {
            var Q0;
            {var subQ0=sQuery(id+"F21.wireOp",EDGE,"E64");var subQ1=makeQuery(id+"F21.imprint","IMPRINT",VERTEX,{"disambiguationData":[OD(0.0)],"derivedFrom":subQ0});Q0=makeQuery(id+"F21.imprint","IMPRINT",FACE,{"disambiguationData":[TD([[makeQuery(id+"F21.imprint","IMPRINT",EDGE,{"disambiguationData":[TD([[subQ1,1.0]])],"derivedFrom":subQ0}),-1.0]])]});}
            extrude(context, id + "F80", {"entities" : qUnion([Q0]), "operationType" : NewBodyOperationType.ADD, "oppositeDirection" : true, "depth" : 25.4 * mm, "offsetDistance" : 25.4 * mm});
        }
        {
            var Q0;
            {var subQ0=sQuery(id+"F21.wireOp",EDGE,"E70");var subQ6=makeQuery(id+"F21.imprint","IMPRINT",EDGE,{"derivedFrom":subQ0});Q0=qUnion([makeQuery(id+"F21.imprint","IMPRINT",FACE,{"disambiguationData":[TD([[subQ6,-1.0]])]}),makeQuery(id+"F21.imprint","IMPRINT",FACE,{"disambiguationData":[TD([[subQ6,1.0]])]})]);}
            extrude(context, id + "F81", {"entities" : qUnion([Q0]), "operationType" : NewBodyOperationType.ADD, "oppositeDirection" : true, "depth" : 635 * mm, "offsetDistance" : 25.4 * mm});
        }
        {
            var Q0;
            Q0=qCreatedBy(makeId("Top.planeOp"),FACE);
            cPlane(context, id + "F82", {"entities" : qUnion([Q0]), "cplaneType" : CPlaneType.OFFSET, "offset" : 807.97 * mm, "width" : 152.4 * mm, "height" : 152.4 * mm});
        }
        {
            var Q0;
            Q0=qCreatedBy(id+"F82.planeOp",FACE);
            var sketch = newSketch(context, id + "F83", { "sketchPlane" : qUnion([Q0])});
            skLineSegment(sketch, "E200", {"start": v(0, -6.77) * mm, "end": v(0, 86.13) * mm});
            skLineSegment(sketch, "E201", {"start": v(-47.49, 106.89) * mm, "end": v(-47.49, 124.67) * mm});
            skLineSegment(sketch, "E202", {"start": v(-47.49, 124.67) * mm, "end": v(54.18, 124.67) * mm});
            skLineSegment(sketch, "E203", {"start": v(54.18, 124.67) * mm, "end": v(54.18, 86.13) * mm});
            skLineSegment(sketch, "E204", {"start": v(54.18, 86.13) * mm, "end": v(-47.49, 86.13) * mm});
            skLineSegment(sketch, "E205", {"start": v(-47.49, 86.13) * mm, "end": v(-47.49, 106.89) * mm});
            skSolve(sketch);
        }
        {
            var Q0;
            Q0=makeQuery(id+"F83.imprint","IMPRINT",FACE,{"disambiguationData":[TD([[makeQuery(id+"F83.imprint","IMPRINT",EDGE,{"derivedFrom":sQuery(id+"F83.wireOp",EDGE,"E201")}),-1.0]])]});
            extrude(context, id + "F84", {"entities" : qUnion([Q0]), "operationType" : NewBodyOperationType.ADD, "depth" : 2.54 * mm, "offsetDistance" : 25.4 * mm});
        }
        {
            var Q0;
            {var subQ1=sQuery(id+"F25.wireOp",EDGE,"E80");Q0=makeQuery(id+"F25.imprint","IMPRINT",FACE,{"disambiguationData":[TD([[makeQuery(id+"F25.imprint","IMPRINT",EDGE,{"derivedFrom":subQ1}),-1.0]])]});}
            extrude(context, id + "F85", {"entities" : qUnion([Q0]), "operationType" : NewBodyOperationType.ADD, "oppositeDirection" : true, "depth" : 25.4 * mm, "offsetDistance" : 25.4 * mm});
        }
        {
            var Q0;
            Q0=makeQuery(id+"F23.imprint","IMPRINT",FACE,{"disambiguationData":[TD([[makeQuery(id+"F23.imprint","IMPRINT",EDGE,{"derivedFrom":sQuery(id+"F23.wireOp",EDGE,"E75")}),1.0]])]});
            extrude(context, id + "F86", {"entities" : qUnion([Q0]), "operationType" : NewBodyOperationType.ADD, "depth" : 12.7 * mm, "offsetDistance" : 25.4 * mm});
        }
        {
            var Q0;
            Q0=makeQuery(id+"F47.imprint","IMPRINT",FACE,{"disambiguationData":[TD([[makeQuery(id+"F47.imprint","IMPRINT",EDGE,{"derivedFrom":sQuery(id+"F47.wireOp",EDGE,"E171")}),1.0]])]});
            extrude(context, id + "F87", {"entities" : qUnion([Q0]), "operationType" : NewBodyOperationType.ADD, "oppositeDirection" : true, "depth" : 431.8 * mm, "offsetDistance" : 25.4 * mm});
        }
        {
            var Q0;
            Q0=qCreatedBy(makeId("Front.planeOp"),FACE);
            cPlane(context, id + "F88", {"entities" : qUnion([Q0]), "cplaneType" : CPlaneType.OFFSET, "offset" : 507.75 * mm, "oppositeDirection" : true, "width" : 152.4 * mm, "height" : 152.4 * mm});
        }
        {
            var Q0;
            Q0=qCreatedBy(id+"F88.planeOp",FACE);
            var sketch = newSketch(context, id + "F89", { "sketchPlane" : qUnion([Q0])});
            skLineSegment(sketch, "E206", {"start": v(0, 0) * mm, "end": v(0, 757.17) * mm});
            skLineSegment(sketch, "E207", {"start": v(0, 807.97) * mm, "end": v(-210.82, 807.97) * mm});
            skLineSegment(sketch, "E208", {"start": v(0, 807.97) * mm, "end": v(212.1, 807.97) * mm});
            skLineSegment(sketch, "E209", {"start": v(0, 0) * mm, "end": v(0, -177.8) * mm});
            skLineSegment(sketch, "E210", {"start": v(379.02, -328.58) * mm, "end": v(212.1, 807.97) * mm});
            skLineSegment(sketch, "E211", {"start": v(-355.6, -177.8) * mm, "end": v(-210.82, 807.97) * mm});
            skLineSegment(sketch, "E212", {"start": v(168.76, 757.17) * mm, "end": v(328.22, -328.58) * mm});
            skLineSegment(sketch, "E213", {"start": v(-167.48, 757.17) * mm, "end": v(-304.8, -177.8) * mm});
            skLineSegment(sketch, "E214", {"start": v(-167.48, 757.17) * mm, "end": v(168.76, 757.17) * mm});
            skLineSegment(sketch, "E215", {"start": v(372.67, -328.58) * mm, "end": v(206.68, 801.62) * mm});
            skLineSegment(sketch, "E216", {"start": v(-349.25, -177.8) * mm, "end": v(-205.4, 801.62) * mm});
            skLineSegment(sketch, "E217", {"start": v(-205.4, 801.62) * mm, "end": v(206.68, 801.62) * mm});
            skLineSegment(sketch, "E218", {"start": v(379.02, -328.58) * mm, "end": v(328.22, -328.58) * mm});
            skLineSegment(sketch, "E219", {"start": v(-210.82, 807.97) * mm, "end": v(-377.75, -328.58) * mm});
            skLineSegment(sketch, "E220", {"start": v(-205.4, 801.62) * mm, "end": v(-371.4, -328.58) * mm});
            skLineSegment(sketch, "E221", {"start": v(-167.48, 757.17) * mm, "end": v(-326.95, -328.58) * mm});
            skLineSegment(sketch, "E222.trimOffspring", {"start": v(-326.95, -328.58) * mm, "end": v(-377.75, -328.58) * mm});
            skSolve(sketch);
        }
        {
            var Q0;
            {var subQ1=sQuery(id+"F89.wireOp",EDGE,"E212");Q0=makeQuery(id+"F89.imprint","IMPRINT",FACE,{"disambiguationData":[TD([[makeQuery(id+"F89.imprint","IMPRINT",EDGE,{"derivedFrom":subQ1}),1.0]])]});}
            extrude(context, id + "F90", {"entities" : qUnion([Q0]), "operationType" : NewBodyOperationType.ADD, "depth" : 6.35 * mm, "offsetDistance" : 25.4 * mm});
        }
        {
            var Q0;
            Q0=makeQuery(id+"F89.imprint","IMPRINT",FACE,{"disambiguationData":[TD([[makeQuery(id+"F89.imprint","IMPRINT",EDGE,{"derivedFrom":sQuery(id+"F89.wireOp",EDGE,"E207")}),1.0]])]});
            extrude(context, id + "F91", {"entities" : qUnion([Q0]), "operationType" : NewBodyOperationType.ADD, "depth" : 50.8 * mm, "offsetDistance" : 25.4 * mm});
        }
        {
            var Q0;
            {var subQ0=sQuery(id+"F47.wireOp",EDGE,"E173");Q0=makeQuery(id+"F47.imprint","IMPRINT",FACE,{"disambiguationData":[TD([[makeQuery(id+"F47.imprint","IMPRINT",EDGE,{"derivedFrom":subQ0}),-1.0]])]});}
            extrude(context, id + "F92", {"entities" : qUnion([Q0]), "operationType" : NewBodyOperationType.ADD, "oppositeDirection" : true, "depth" : 431.8 * mm, "offsetDistance" : 25.4 * mm});
        }
        {
            var Q0;
            {var subQ2=sQuery(id+"F47.wireOp",EDGE,"E183");Q0=makeQuery(id+"F47.imprint","IMPRINT",FACE,{"disambiguationData":[TD([[makeQuery(id+"F47.imprint","IMPRINT",EDGE,{"derivedFrom":subQ2}),-1.0]])]});}
            extrude(context, id + "F93", {"entities" : qUnion([Q0]), "operationType" : NewBodyOperationType.ADD, "oppositeDirection" : true, "depth" : 50.8 * mm, "offsetDistance" : 25.4 * mm});
        }
        {
            var Q0;
            Q0=qCreatedBy(id+"F82.planeOp",FACE);
            var sketch = newSketch(context, id + "F94", { "sketchPlane" : qUnion([Q0])});
            skLineSegment(sketch, "E223", {"start": v(0, 0) * mm, "end": v(0, 466.84) * mm});
            skLineSegment(sketch, "E224", {"start": v(40.83, 485.11) * mm, "end": v(40.83, 466.84) * mm});
            skLineSegment(sketch, "E225", {"start": v(40.83, 466.84) * mm, "end": v(-41.87, 466.84) * mm});
            skLineSegment(sketch, "E226", {"start": v(-41.87, 466.84) * mm, "end": v(-41.87, 484.55) * mm});
            skLineSegment(sketch, "E227", {"start": v(40.83, 485.11) * mm, "end": v(40.83, 501.53) * mm});
            skLineSegment(sketch, "E228", {"start": v(40.83, 501.53) * mm, "end": v(-42.6, 500.4) * mm});
            skLineSegment(sketch, "E229", {"start": v(-42.6, 500.4) * mm, "end": v(-41.87, 484.55) * mm});
            skSolve(sketch);
        }
        {
            var Q0;
            {var subQ3=sQuery(id+"F94.wireOp",EDGE,"E224");Q0=makeQuery(id+"F94.imprint","IMPRINT",FACE,{"disambiguationData":[TD([[makeQuery(id+"F94.imprint","IMPRINT",EDGE,{"derivedFrom":subQ3}),-1.0]])]});}
            extrude(context, id + "F95", {"entities" : qUnion([Q0]), "operationType" : NewBodyOperationType.ADD, "depth" : 2.54 * mm, "offsetDistance" : 25.4 * mm});
        }
        {
            var Q0;
            Q0=qCreatedBy(makeId("Front.planeOp"),FACE);
            cPlane(context, id + "F96", {"entities" : qUnion([Q0]), "cplaneType" : CPlaneType.OFFSET, "offset" : 482.6 * mm, "oppositeDirection" : true, "width" : 152.4 * mm, "height" : 152.4 * mm});
        }
        {
            var Q0;
            Q0=qCreatedBy(id+"F96.planeOp",FACE);
            var sketch = newSketch(context, id + "F97", { "sketchPlane" : qUnion([Q0])});
            skLineSegment(sketch, "E230", {"start": v(-0.3, 808.83) * mm, "end": v(-38.4, 808.83) * mm});
            skLineSegment(sketch, "E231", {"start": v(-38.4, 808.83) * mm, "end": v(-38.4, 821.53) * mm});
            skLineSegment(sketch, "E232", {"start": v(-38.4, 821.53) * mm, "end": v(-25.7, 821.53) * mm});
            skLineSegment(sketch, "E233", {"start": v(-0.3, 808.83) * mm, "end": v(37.8, 808.83) * mm});
            skLineSegment(sketch, "E234", {"start": v(37.8, 808.83) * mm, "end": v(37.8, 821.53) * mm});
            skLineSegment(sketch, "E235", {"start": v(37.8, 821.53) * mm, "end": v(25.1, 821.53) * mm});
            skPoint(sketch, "E236", {"position": v(0, 872.34) * mm});
            skArc(sketch, "E237", {"start": v(25.1, 821.53) * mm, "mid": v(-0.3, 872.34) * mm, "end": v(-25.7, 821.53) * mm});
            skCircle(sketch, "E238", {"center": v(-0.3, 840.59) * mm, "radius": 19.05 * mm});
            skSolve(sketch);
        }
        {
            var Q0;
            Q0=makeQuery(id+"F97.imprint","IMPRINT",FACE,{"disambiguationData":[TD([[makeQuery(id+"F97.imprint","IMPRINT",EDGE,{"derivedFrom":sQuery(id+"F97.wireOp",EDGE,"E230")}),-1.0]])]});
            extrude(context, id + "F98", {"entities" : qUnion([Q0]), "operationType" : NewBodyOperationType.ADD, "depth" : 12.7 * mm, "offsetDistance" : 25.4 * mm});
        }
        {
            var Q0;
            Q0=makeQuery(id+"F97.imprint","IMPRINT",FACE,{"disambiguationData":[TD([[makeQuery(id+"F97.imprint","IMPRINT",EDGE,{"derivedFrom":sQuery(id+"F97.wireOp",EDGE,"E230")}),-1.0]])]});
            extrude(context, id + "F99", {"entities" : qUnion([Q0]), "operationType" : NewBodyOperationType.ADD, "oppositeDirection" : true, "depth" : 12.7 * mm, "offsetDistance" : 25.4 * mm});
        }
        {
            var Q0;
            Q0=qCreatedBy(makeId("Front.planeOp"),FACE);
            cPlane(context, id + "F100", {"entities" : qUnion([Q0]), "cplaneType" : CPlaneType.OFFSET, "offset" : 571.5 * mm, "oppositeDirection" : true, "width" : 152.4 * mm, "height" : 152.4 * mm});
        }
        {
            var Q0;
            Q0=qCreatedBy(id+"F100.planeOp",FACE);
            var sketch = newSketch(context, id + "F101", { "sketchPlane" : qUnion([Q0])});
            skLineSegment(sketch, "E239", {"start": v(0, 0) * mm, "end": v(0, 713.59) * mm});
            skCircle(sketch, "E240", {"center": v(0, 840.59) * mm, "radius": 127 * mm});
            skLineSegment(sketch, "E241", {"start": v(0, 859.64) * mm, "end": v(0, 840.59) * mm});
            skCircle(sketch, "E242", {"center": v(0, 840.59) * mm, "radius": 19.05 * mm});
            skPoint(sketch, "E243.orphan", {"position": v(0, 967.59) * mm});
            skLineSegment(sketch, "E244.trimOffspring", {"start": v(0, 821.54) * mm, "end": v(0, 840.59) * mm});
            skSolve(sketch);
        }
        {
            var Q0;
            Q0=makeQuery(id+"F101.imprint","IMPRINT",FACE,{"disambiguationData":[TD([[makeQuery(id+"F101.imprint","IMPRINT",EDGE,{"derivedFrom":sQuery(id+"F101.wireOp",EDGE,"E240")}),1.0]])]});
            extrude(context, id + "F102", {"entities" : qUnion([Q0]), "operationType" : NewBodyOperationType.ADD, "oppositeDirection" : true, "depth" : 38.1 * mm, "offsetDistance" : 25.4 * mm});
        }
        {
            var Q0;
            Q0=qCreatedBy(makeId("Front.planeOp"),FACE);
            cPlane(context, id + "F103", {"entities" : qUnion([Q0]), "cplaneType" : CPlaneType.OFFSET, "offset" : 558.8 * mm, "oppositeDirection" : true, "width" : 152.4 * mm, "height" : 152.4 * mm});
        }
        {
            var Q0;
            Q0=qCreatedBy(id+"F103.planeOp",FACE);
            var sketch = newSketch(context, id + "F104", { "sketchPlane" : qUnion([Q0])});
            skLineSegment(sketch, "E245", {"start": v(0, 0) * mm, "end": v(0, 840.59) * mm});
            skCircle(sketch, "E246", {"center": v(0, 840.59) * mm, "radius": 146.05 * mm});
            skSolve(sketch);
        }
        {
            var Q0;
            Q0=makeQuery(id+"F104.imprint","IMPRINT",FACE,{"disambiguationData":[TD([[makeQuery(id+"F104.imprint","IMPRINT",EDGE,{"derivedFrom":sQuery(id+"F104.wireOp",EDGE,"E246")}),1.0]])]});
            extrude(context, id + "F105", {"entities" : qUnion([Q0]), "operationType" : NewBodyOperationType.ADD, "oppositeDirection" : true, "depth" : 12.7 * mm, "offsetDistance" : 25.4 * mm});
        }
        {
            var Q0;
            Q0=qCreatedBy(makeId("Front.planeOp"),FACE);
            cPlane(context, id + "F106", {"entities" : qUnion([Q0]), "cplaneType" : CPlaneType.OFFSET, "offset" : 607.06 * mm, "oppositeDirection" : true, "width" : 152.4 * mm, "height" : 152.4 * mm});
        }
        {
            var Q0;
            Q0=qCreatedBy(id+"F106.planeOp",FACE);
            var sketch = newSketch(context, id + "F107", { "sketchPlane" : qUnion([Q0])});
            skLineSegment(sketch, "E247", {"start": v(0, 0) * mm, "end": v(0, 840.59) * mm});
            skCircle(sketch, "E248", {"center": v(0, 840.59) * mm, "radius": 146.05 * mm});
            skSolve(sketch);
        }
        {
            var Q0;
            Q0=makeQuery(id+"F107.imprint","IMPRINT",FACE,{"disambiguationData":[TD([[makeQuery(id+"F107.imprint","IMPRINT",EDGE,{"derivedFrom":sQuery(id+"F107.wireOp",EDGE,"E248")}),1.0]])]});
            extrude(context, id + "F108", {"entities" : qUnion([Q0]), "operationType" : NewBodyOperationType.ADD, "oppositeDirection" : true, "depth" : 15.24 * mm, "offsetDistance" : 25.4 * mm});
        }
        {
            var Q0;
            Q0=makeQuery(id+"F37.imprint","IMPRINT",FACE,{"disambiguationData":[TD([[makeQuery(id+"F37.imprint","IMPRINT",EDGE,{"derivedFrom":sQuery(id+"F37.wireOp",EDGE,"E140")}),1.0]])]});
            extrude(context, id + "F109", {"entities" : qUnion([Q0]), "operationType" : NewBodyOperationType.ADD, "depth" : 127 * mm, "offsetDistance" : 25.4 * mm});
        }
        {
            var Q0;
            Q0=makeQuery(id+"F37.imprint","IMPRINT",FACE,{"disambiguationData":[TD([[makeQuery(id+"F37.imprint","IMPRINT",EDGE,{"derivedFrom":sQuery(id+"F37.wireOp",EDGE,"E140")}),1.0]])]});
            extrude(context, id + "F110", {"entities" : qUnion([Q0]), "operationType" : NewBodyOperationType.ADD, "oppositeDirection" : true, "depth" : 177.8 * mm, "offsetDistance" : 25.4 * mm});
        }
    });
